# Revit family: Gessi_INCISO-ACCESSORI-Black-standing-brush-ho
name_source: partatom
category: Plumbing Fixtures
revit_build: Autodesk Revit 2018 (Build: 20190510_1515(x64)
units: mm (PartAtom-declared; Revit-internal decimal feet)

## family parameters
Always vertical = No
Cut with Voids When Loaded = No
OmniClass Number = 23.31.11.00
OmniClass Title = Faucets
Part Type = Normal
Room Calculation Point = No
Round Connector Dimension = Use Diameter
Shared = No
Work Plane-Based = No

## types (14) — shared parameters
Brand url = http://www.gessi.it
Ceramic - Black = Gessi - Ceramic - Black
Description = Black standing brush holder
Design country = Italy
Edition number = 1
IFC Classification = Sanitary Terminal
Installation instructions = https://www.gessi.com
Manufacturer = Gessi
Manufacturer country = Italy
Manufacturer name = Gessi
Model = 58544
Product Guid = adde5842-c5ed-4589-990f-83af46b739c0
Product SKU = 58544
Product certification = https://www.gessi.com
Product data url = https://bimobject.com
Product family = INCISO
Product group = INCISO ACCESSORI
Product name = INCISO ACCESSORI - Black standing brush holder - 58544
Product url = https://www.gessi.com
QR code = http://bimobject.com
Technical description = https://www.gessi.com
URL = http://www.gessi.it

## per-type parameters (varying)
| type | Faucet Material |
| Aged Bronze | Gessi - Metal - Aged Bronze |
| Antique Brass | Gessi - Metal - Antique Brass |
| Black Metal | Gessi - Metal - Black Metal |
| Black Metal Brushed | Gessi - Metal - Black Metal Brushed |
| Brass | Gessi - Metal - Brass |
| Brass Brushed | Gessi - Metal - Brass Brushed |
| Chrome | Gessi - Metal - Chrome |
| Copper | Gessi - Metal - Copper |
| Copper Brushed | Gessi - Metal - Copper Brushed |
| Finox | Gessi - Metal - Finox |
| Matte Black | Gessi - Metal - Matte Black |
| Nickel | Gessi - Metal - Nickel |
| Warm Bronze | Gessi - Metal - Warm Bronze |
| Warm Bronze Brushed | Gessi - Metal - Warm Bronze Brushed |

## geometry (parser evidence)
native form markers: Sweep x4
no freeform markers — native parametric forms only
